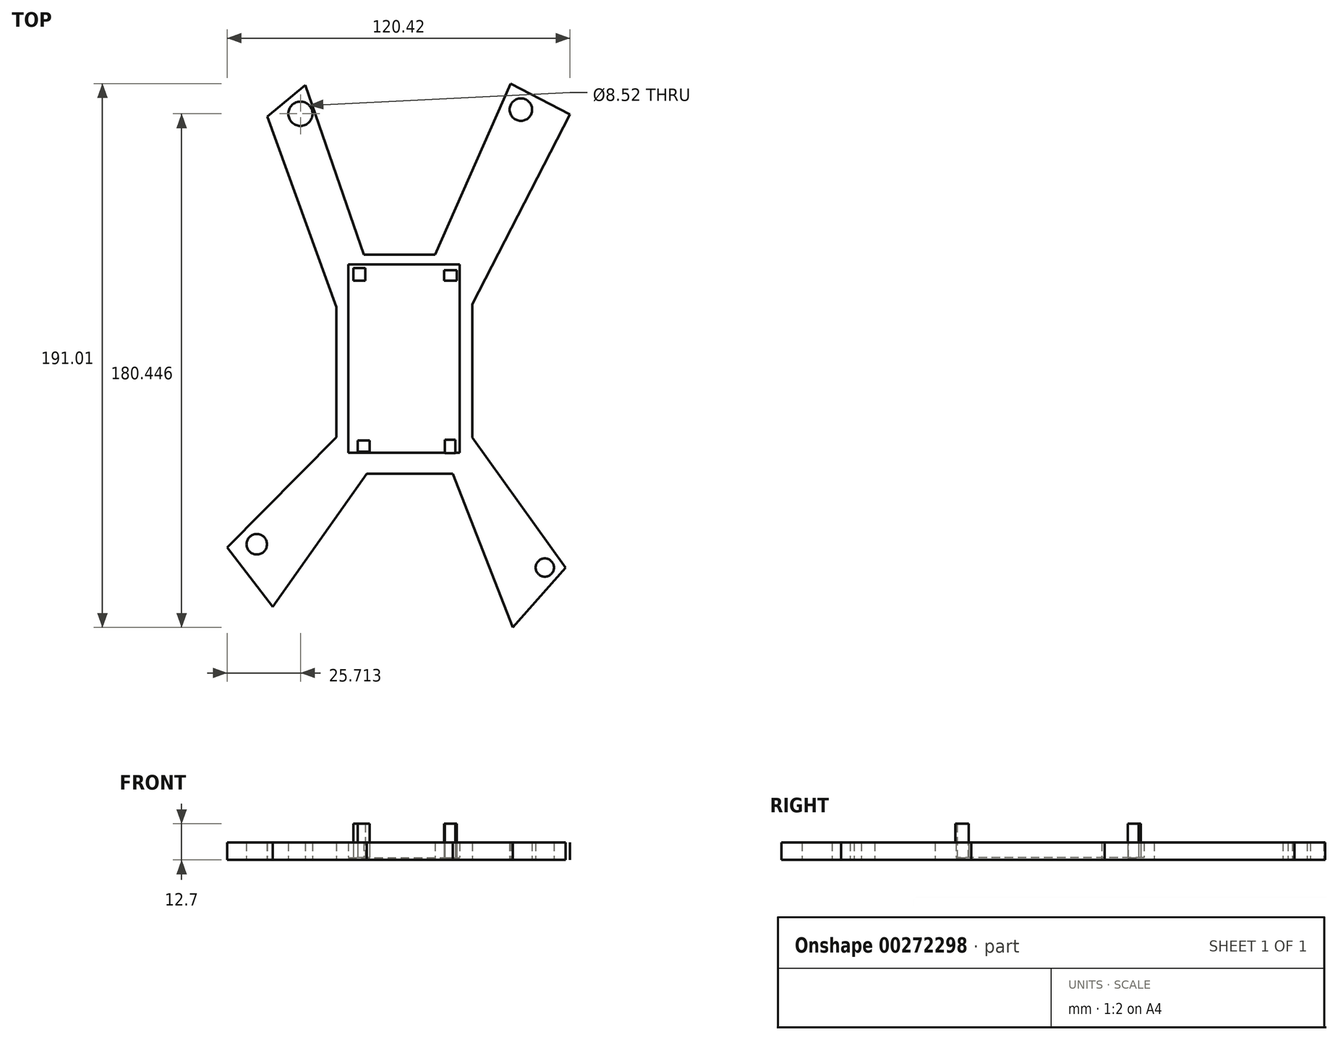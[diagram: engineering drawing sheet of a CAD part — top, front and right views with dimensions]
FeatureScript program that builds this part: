
annotation { "Feature Type Name" : "Feature", "Feature Type Description" : "" }
export const myFeature = defineFeature(function(context is Context, id is Id, definition is map)
    precondition{}
    {
        {
            var Q0;
            Q0=qCreatedBy(makeId("Top.planeOp"),FACE);
            var sketch = newSketch(context, id + "F0", { "sketchPlane" : qUnion([Q0])});
            skLineSegment(sketch, "E0.bottom", {"start": v(-20.77, 33.76) * mm, "end": v(26.91, 33.76) * mm});
            skLineSegment(sketch, "E0.top", {"start": v(-20.77, -43.2) * mm, "end": v(26.91, -43.2) * mm});
            skLineSegment(sketch, "E0.left", {"start": v(-20.77, 33.76) * mm, "end": v(-20.77, -43.2) * mm});
            skLineSegment(sketch, "E0.right", {"start": v(26.91, 33.76) * mm, "end": v(26.91, -43.2) * mm});
            skLineSegment(sketch, "E1", {"start": v(-11.1, 33.76) * mm, "end": v(-31.7, 93.32) * mm});
            skLineSegment(sketch, "E2", {"start": v(-31.7, 93.32) * mm, "end": v(-45.01, 82.22) * mm});
            skLineSegment(sketch, "E3", {"start": v(-45.01, 82.22) * mm, "end": v(-20.77, 15.34) * mm});
            skLineSegment(sketch, "E4", {"start": v(-20.77, 15.34) * mm, "end": v(-20.77, -43.2) * mm});
            skLineSegment(sketch, "E5", {"start": v(-10.08, -43.2) * mm, "end": v(-43.21, -89.97) * mm});
            skLineSegment(sketch, "E6", {"start": v(-43.21, -89.97) * mm, "end": v(-59.14, -69.16) * mm});
            skLineSegment(sketch, "E7", {"start": v(-59.14, -69.16) * mm, "end": v(-20.77, -30.43) * mm});
            skLineSegment(sketch, "E8", {"start": v(-20.77, -30.43) * mm, "end": v(-20.77, -43.2) * mm});
            skLineSegment(sketch, "E9", {"start": v(20.07, -43.2) * mm, "end": v(41.12, -97.23) * mm});
            skLineSegment(sketch, "E10", {"start": v(41.12, -97.23) * mm, "end": v(59.7, -76.22) * mm});
            skLineSegment(sketch, "E11", {"start": v(59.7, -76.22) * mm, "end": v(26.91, -30.5) * mm});
            skLineSegment(sketch, "E12", {"start": v(26.91, -30.5) * mm, "end": v(26.91, 33.76) * mm});
            skLineSegment(sketch, "E13", {"start": v(26.91, 16.3) * mm, "end": v(61.28, 83.01) * mm});
            skLineSegment(sketch, "E14", {"start": v(61.28, 83.01) * mm, "end": v(40.37, 93.78) * mm});
            skLineSegment(sketch, "E15", {"start": v(40.37, 93.78) * mm, "end": v(13.82, 33.76) * mm});
            skLineSegment(sketch, "E16", {"start": v(13.82, 33.76) * mm, "end": v(26.91, 33.76) * mm});
            skCircle(sketch, "E17", {"center": v(-48.77, -68.03) * mm, "radius": 3.6 * mm});
            skCircle(sketch, "E18", {"center": v(52.42, -76.22) * mm, "radius": 3.2 * mm});
            skCircle(sketch, "E19", {"center": v(44.02, 84.68) * mm, "radius": 3.95 * mm});
            skCircle(sketch, "E20", {"center": v(-33.43, 83.22) * mm, "radius": 4.26 * mm});
            skLineSegment(sketch, "E21.bottom", {"start": v(-16.62, 30.24) * mm, "end": v(22.47, 30.24) * mm});
            skLineSegment(sketch, "E21.top", {"start": v(-16.62, -35.88) * mm, "end": v(22.47, -35.88) * mm});
            skLineSegment(sketch, "E21.left", {"start": v(-16.62, 30.24) * mm, "end": v(-16.62, -35.88) * mm});
            skLineSegment(sketch, "E21.right", {"start": v(22.47, 30.24) * mm, "end": v(22.47, -35.88) * mm});
            skSolve(sketch);
        }
        {
            var Q0;
            Q0=makeQuery(id+"F0.imprint","IMPRINT",FACE,{"disambiguationData":[TD([[makeQuery(id+"F0.imprint","IMPRINT",EDGE,{"derivedFrom":sQuery(id+"F0.wireOp",EDGE,"E21.bottom")}),-1.0]])]});
            extrude(context, id + "F1", {"entities" : qUnion([Q0]), "depth" : 0.76 * mm});
        }
        {
            var Q0;
            Q0 = qSketchRegion(id + "F0", true);
            extrude(context, id + "F2", {"entities" : qUnion([Q0]), "operationType" : NewBodyOperationType.ADD, "depth" : 6.1 * mm});
        }
        {
            var Q0;
            Q0=qCreatedBy(makeId("Top.planeOp"),FACE);
            var sketch = newSketch(context, id + "F3", { "sketchPlane" : qUnion([Q0])});
            skLineSegment(sketch, "E22.bottom", {"start": v(-14.9, 29.02) * mm, "end": v(-10.58, 29.02) * mm});
            skLineSegment(sketch, "E22.top", {"start": v(-14.9, 24.58) * mm, "end": v(-10.58, 24.58) * mm});
            skLineSegment(sketch, "E22.left", {"start": v(-14.9, 29.02) * mm, "end": v(-14.9, 24.58) * mm});
            skLineSegment(sketch, "E22.right", {"start": v(-10.58, 29.02) * mm, "end": v(-10.58, 24.58) * mm});
            skLineSegment(sketch, "E23.bottom", {"start": v(21.54, 28.26) * mm, "end": v(17, 28.26) * mm});
            skLineSegment(sketch, "E23.top", {"start": v(21.54, 24.55) * mm, "end": v(17, 24.55) * mm});
            skLineSegment(sketch, "E23.left", {"start": v(21.54, 28.26) * mm, "end": v(21.54, 24.55) * mm});
            skLineSegment(sketch, "E23.right", {"start": v(17, 28.26) * mm, "end": v(17, 24.55) * mm});
            skLineSegment(sketch, "E24.bottom", {"start": v(20.98, -31.32) * mm, "end": v(17.28, -31.32) * mm});
            skLineSegment(sketch, "E24.top", {"start": v(20.98, -36.02) * mm, "end": v(17.28, -36.02) * mm});
            skLineSegment(sketch, "E24.left", {"start": v(20.98, -31.32) * mm, "end": v(20.98, -36.02) * mm});
            skLineSegment(sketch, "E24.right", {"start": v(17.28, -31.32) * mm, "end": v(17.28, -36.02) * mm});
            skLineSegment(sketch, "E25.bottom", {"start": v(-13.3, -31.6) * mm, "end": v(-9.12, -31.6) * mm});
            skLineSegment(sketch, "E25.top", {"start": v(-13.3, -35.47) * mm, "end": v(-9.12, -35.47) * mm});
            skLineSegment(sketch, "E25.left", {"start": v(-13.3, -31.6) * mm, "end": v(-13.3, -35.47) * mm});
            skLineSegment(sketch, "E25.right", {"start": v(-9.12, -31.6) * mm, "end": v(-9.12, -35.47) * mm});
            skSolve(sketch);
        }
        {
            var Q0;
            Q0 = qSketchRegion(id + "F3", true);
            extrude(context, id + "F4", {"entities" : qUnion([Q0]), "operationType" : NewBodyOperationType.ADD, "depth" : 12.7 * mm});
        }
    });
